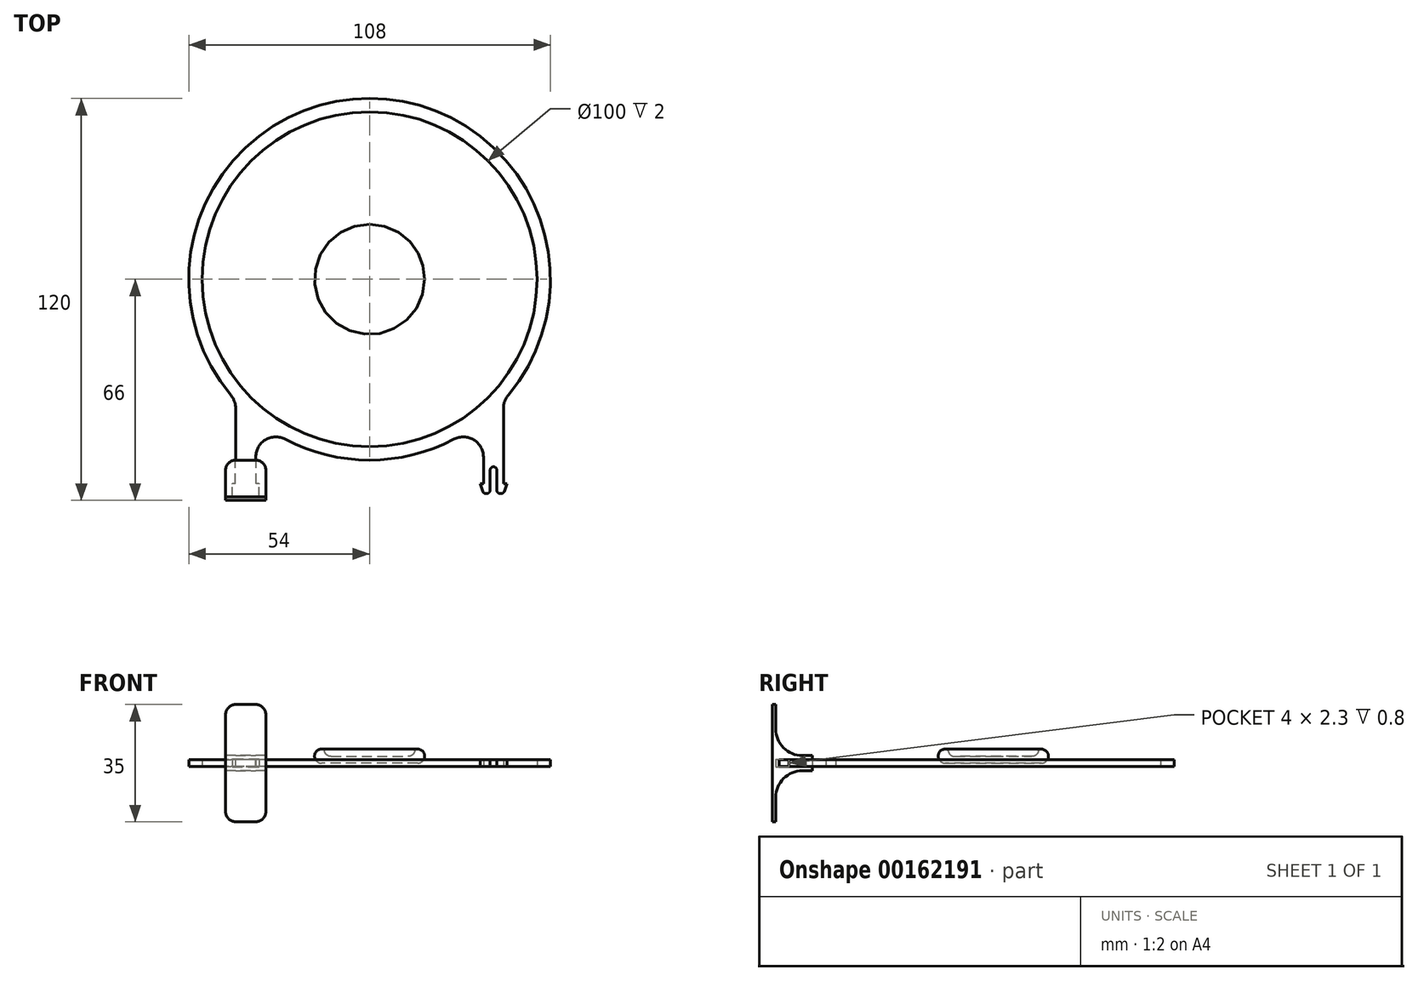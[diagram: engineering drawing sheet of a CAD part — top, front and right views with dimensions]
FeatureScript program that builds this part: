
annotation { "Feature Type Name" : "Feature", "Feature Type Description" : "" }
export const myFeature = defineFeature(function(context is Context, id is Id, definition is map)
    precondition{}
    {
        {
            var Q0;
            Q0=qCreatedBy(makeId("Front.planeOp"),FACE);
            var sketch = newSketch(context, id + "F0", { "sketchPlane" : qUnion([Q0])});
            skLineSegment(sketch, "E0", {"start": v(0, 0) * mm, "end": v(-14.35, 0) * mm});
            skArc(sketch, "E1", {"start": v(-14.35, 4.2) * mm, "mid": v(-16.45, 2.1) * mm, "end": v(-14.35, 0) * mm});
            skLineSegment(sketch, "E2", {"start": v(-14.35, 4.2) * mm, "end": v(-13.5, 4.2) * mm});
            skLineSegment(sketch, "E3", {"start": v(-13.5, 4.2) * mm, "end": v(-13.5, 2) * mm});
            skLineSegment(sketch, "E4", {"start": v(-13.5, 2) * mm, "end": v(0, 2) * mm});
            skLineSegment(sketch, "E5", {"start": v(0, 2) * mm, "end": v(0, 0) * mm});
            skSolve(sketch);
        }
        {
            var Q0;
            Q0=makeQuery(id+"F0.imprint","IMPRINT",FACE,{"disambiguationData":[TD([[makeQuery(id+"F0.imprint","IMPRINT",EDGE,{"derivedFrom":sQuery(id+"F0.wireOp",EDGE,"E0")}),-1.0]])]});
            var Q1;
            Q1=sQuery(id+"F0.wireOp",EDGE,"E5");
            revolve(context, id + "F1", {"entities" : qUnion([Q0]), "axis" : qUnion([Q1]), "revolveType" : RevolveType.FULL});
        }
        {
            var Q0;
            Q0=makeQuery(id+"F1.opRevolve","SWEPT_EDGE",EDGE,{"disambiguationData":[OSD([sQuery(id+"F0.wireOp",EDGE,"E2"),sQuery(id+"F0.wireOp",EDGE,"E3")])]});
            fillet(context, id + "F2", {"entities" : qUnion([Q0]), "radius" : .5 * mm, "tangentPropagation" : true, "allowEdgeOverflow" : false});
        }
        {
            var Q0;
            Q0=makeQuery(id+"F1.opRevolve","SWEPT_EDGE",EDGE,{"disambiguationData":[OSD([sQuery(id+"F0.wireOp",EDGE,"E3"),sQuery(id+"F0.wireOp",EDGE,"E4")])]});
            fillet(context, id + "F3", {"entities" : qUnion([Q0]), "radius" : 2 * mm, "tangentPropagation" : true, "allowEdgeOverflow" : false});
        }
        {
            var Q0;
            Q0=qCreatedBy(makeId("Top.planeOp"),FACE);
            var sketch = newSketch(context, id + "F4", { "sketchPlane" : qUnion([Q0])});
            skCircle(sketch, "E6", {"center": v(0, 0) * mm, "radius": 50 * mm});
            skCircle(sketch, "E7.0", {"center": v(0, 0) * mm, "radius": 54 * mm});
            skLineSegment(sketch, "E8", {"start": v(-40, -36.28) * mm, "end": v(-40, -61) * mm});
            skLineSegment(sketch, "E9", {"start": v(-39.28, -64) * mm, "end": v(-39, -64) * mm});
            skLineSegment(sketch, "E10", {"start": v(-38, -63) * mm, "end": v(-38, -57) * mm});
            skLineSegment(sketch, "E11", {"start": v(-37, -56) * mm, "end": v(-37, -56) * mm});
            skLineSegment(sketch, "E12", {"start": v(-36, -57) * mm, "end": v(-36, -63) * mm});
            skLineSegment(sketch, "E13", {"start": v(-35, -64) * mm, "end": v(-34.72, -64) * mm});
            skLineSegment(sketch, "E14", {"start": v(-34, -61) * mm, "end": v(-34, -41.95) * mm});
            skLineSegment(sketch, "E15", {"start": v(-40, -64.59) * mm, "end": v(-40, -64.59) * mm});
            skLineSegment(sketch, "E16", {"start": v(-40, -61) * mm, "end": v(-41, -61) * mm});
            skLineSegment(sketch, "E17", {"start": v(-41, -61) * mm, "end": v(-40.23, -63.32) * mm});
            skLineSegment(sketch, "E18", {"start": v(-37, -56) * mm, "end": v(-37, -64) * mm, "construction": true});
            skLineSegment(sketch, "E19.MirrorCS", {"start": v(-33, -61) * mm, "end": v(-34, -64) * mm});
            skLineSegment(sketch, "E20.MirrorCS", {"start": v(-33, -61) * mm, "end": v(-33.77, -63.32) * mm});
            skLineSegment(sketch, "E21.MirrorCS", {"start": v(-34, -61) * mm, "end": v(-33, -61) * mm});
            skLineSegment(sketch, "E22", {"start": v(0, 0) * mm, "end": v(0, -62.97) * mm, "construction": true});
            skPoint(sketch, "E23.visualSharp", {"position": v(-38, -56) * mm});
            skArc(sketch, "E23.filletArc", {"start": v(-37, -56) * mm, "mid": v(-37.7, -56.3) * mm, "end": v(-38, -57) * mm});
            skPoint(sketch, "E24.visualSharp", {"position": v(-36, -56) * mm});
            skArc(sketch, "E24.filletArc", {"start": v(-36, -57) * mm, "mid": v(-36.3, -56.3) * mm, "end": v(-37, -56) * mm});
            skPoint(sketch, "E25.visualSharp", {"position": v(-38, -64) * mm});
            skArc(sketch, "E25.filletArc", {"start": v(-39, -64) * mm, "mid": v(-38.3, -63.7) * mm, "end": v(-38, -63) * mm});
            skPoint(sketch, "E26.visualSharp", {"position": v(-40, -64) * mm});
            skArc(sketch, "E26.filletArc", {"start": v(-40.23, -63.32) * mm, "mid": v(-39.86, -63.81) * mm, "end": v(-39.28, -64) * mm});
            skPoint(sketch, "E27.visualSharp", {"position": v(-36, -64) * mm});
            skArc(sketch, "E27.filletArc", {"start": v(-36, -63) * mm, "mid": v(-35.7, -63.7) * mm, "end": v(-35, -64) * mm});
            skPoint(sketch, "E28.visualSharp", {"position": v(-34, -64) * mm});
            skArc(sketch, "E28.filletArc", {"start": v(-34.72, -64) * mm, "mid": v(-34.14, -63.81) * mm, "end": v(-33.77, -63.32) * mm});
            skLineSegment(sketch, "E29.MirrorCS", {"start": v(36, -57) * mm, "end": v(36, -63) * mm});
            skPoint(sketch, "E30.MirrorP", {"position": v(38, -64) * mm});
            skLineSegment(sketch, "E31.MirrorCS", {"start": v(33, -61) * mm, "end": v(34, -64) * mm});
            skLineSegment(sketch, "E32.MirrorCS", {"start": v(40, -36.28) * mm, "end": v(40, -61) * mm});
            skArc(sketch, "E33.MirrorCS", {"start": v(36, -57) * mm, "mid": v(36.3, -56.3) * mm, "end": v(37, -56) * mm});
            skLineSegment(sketch, "E34.MirrorCS", {"start": v(40, -61) * mm, "end": v(41, -61) * mm});
            skLineSegment(sketch, "E35.MirrorCS", {"start": v(35, -64) * mm, "end": v(34.72, -64) * mm});
            skLineSegment(sketch, "E36.MirrorCS", {"start": v(34, -61) * mm, "end": v(33, -61) * mm});
            skArc(sketch, "E37.MirrorCS", {"start": v(40.23, -63.32) * mm, "mid": v(39.86, -63.81) * mm, "end": v(39.28, -64) * mm});
            skLineSegment(sketch, "E38.MirrorCS", {"start": v(33, -61) * mm, "end": v(33.77, -63.32) * mm});
            skLineSegment(sketch, "E39.MirrorCS", {"start": v(39.28, -64) * mm, "end": v(39, -64) * mm});
            skPoint(sketch, "E40.MirrorP", {"position": v(40, -64) * mm});
            skLineSegment(sketch, "E41.MirrorCS", {"start": v(41, -61) * mm, "end": v(40.23, -63.32) * mm});
            skArc(sketch, "E42.MirrorCS", {"start": v(37, -56) * mm, "mid": v(37.7, -56.3) * mm, "end": v(38, -57) * mm});
            skArc(sketch, "E43.MirrorCS", {"start": v(34.72, -64) * mm, "mid": v(34.14, -63.81) * mm, "end": v(33.77, -63.32) * mm});
            skPoint(sketch, "E44.MirrorP", {"position": v(36, -64) * mm});
            skLineSegment(sketch, "E45.MirrorCS", {"start": v(38, -63) * mm, "end": v(38, -57) * mm});
            skPoint(sketch, "E46.MirrorP", {"position": v(38, -56) * mm});
            skArc(sketch, "E47.MirrorCS", {"start": v(39, -64) * mm, "mid": v(38.3, -63.7) * mm, "end": v(38, -63) * mm});
            skLineSegment(sketch, "E48.MirrorCS", {"start": v(37, -56) * mm, "end": v(37, -64) * mm, "construction": true});
            skPoint(sketch, "E49.MirrorP", {"position": v(34, -64) * mm});
            skLineSegment(sketch, "E50.MirrorCS", {"start": v(34, -61) * mm, "end": v(34, -41.95) * mm});
            skPoint(sketch, "E51.MirrorP", {"position": v(36, -56) * mm});
            skArc(sketch, "E52.MirrorCS", {"start": v(36, -63) * mm, "mid": v(35.7, -63.7) * mm, "end": v(35, -64) * mm});
            skSolve(sketch);
        }
        {
            var Q0;
            Q0=makeQuery(id+"F4.imprint","IMPRINT",FACE,{"disambiguationData":[TD([[makeQuery(id+"F4.imprint","IMPRINT",EDGE,{"derivedFrom":sQuery(id+"F4.wireOp",EDGE,"E6")}),-1.0]])]});
            var Q1;
            {var subQ1=sQuery(id+"F4.wireOp",EDGE,"E8");Q1=makeQuery(id+"F4.imprint","IMPRINT",FACE,{"disambiguationData":[TD([[makeQuery(id+"F4.imprint","IMPRINT",EDGE,{"derivedFrom":subQ1}),1.0]])]});}
            var Q2;
            Q2=makeQuery(id+"F4.imprint","IMPRINT",FACE,{"disambiguationData":[TD([[makeQuery(id+"F4.imprint","IMPRINT",EDGE,{"derivedFrom":sQuery(id+"F4.wireOp",EDGE,"E29.MirrorCS")}),-1.0]])]});
            extrude(context, id + "F5", {"entities" : qUnion([Q0, Q1, Q2]), "endBound" : BoundingType.SYMMETRIC, "depth" : 2 * mm});
        }
        {
            var Q0;
            Q0=makeQuery(id+"F5.opExtrude","SWEPT_EDGE",EDGE,{"disambiguationData":[OSD([sQuery(id+"F4.wireOp",EDGE,"E7.0"),sQuery(id+"F4.wireOp",EDGE,"E14")])]});
            var Q1;
            Q1=makeQuery(id+"F5.opExtrude","SWEPT_EDGE",EDGE,{"disambiguationData":[OSD([sQuery(id+"F4.wireOp",EDGE,"E7.0"),sQuery(id+"F4.wireOp",EDGE,"E8")])]});
            var Q2;
            Q2=makeQuery(id+"F5.opExtrude","SWEPT_EDGE",EDGE,{"disambiguationData":[OSD([sQuery(id+"F4.wireOp",EDGE,"E7.0"),sQuery(id+"F4.wireOp",EDGE,"4878f873-84f6-49e9-9cc4-d92dd95d19830.MirrorCS")])]});
            var Q3;
            Q3=makeQuery(id+"F5.opExtrude","SWEPT_EDGE",EDGE,{"disambiguationData":[OSD([sQuery(id+"F4.wireOp",EDGE,"E7.0"),sQuery(id+"F4.wireOp",EDGE,"32b12c6d-282c-4cf4-9ab3-73add998abeb0.MirrorCS")])]});
            fillet(context, id + "F6", {"entities" : qUnion([Q0, Q1, Q2, Q3]), "radius" : 6 * mm, "tangentPropagation" : true, "allowEdgeOverflow" : false});
        }
        {
            var Q0;
            Q0=qCreatedBy(makeId("Top.planeOp"),FACE);
            var sketch = newSketch(context, id + "F7", { "sketchPlane" : qUnion([Q0])});
            skLineSegment(sketch, "E53.bottom", {"start": v(-43, -66) * mm, "end": v(-31, -66) * mm});
            skLineSegment(sketch, "E53.top", {"start": v(-43, -54) * mm, "end": v(-31, -54) * mm});
            skLineSegment(sketch, "E53.left", {"start": v(-43, -66) * mm, "end": v(-43, -54) * mm});
            skLineSegment(sketch, "E53.right", {"start": v(-31, -66) * mm, "end": v(-31, -54) * mm});
            skPoint(sketch, "E53.middle", {"position": v(-37, -60) * mm});
            skPoint(sketch, "E54", {"position": v(-37, -57) * mm});
            skSolve(sketch);
        }
        {
            var Q0;
            Q0=makeQuery(id+"F7.imprint","IMPRINT",FACE,{"disambiguationData":[TD([[makeQuery(id+"F7.imprint","IMPRINT",EDGE,{"derivedFrom":sQuery(id+"F7.wireOp",EDGE,"E53.bottom")}),1.0]])]});
            extrude(context, id + "F8", {"entities" : qUnion([Q0]), "endBound" : BoundingType.SYMMETRIC, "depth" : 4.5 * mm});
        }
        {
            var Q0;
            Q0=makeQuery(id+"F8.opExtrude","SWEPT_FACE",FACE,{"disambiguationData":[OSD([sQuery(id+"F7.wireOp",EDGE,"E53.top")])]});
            var sketch = newSketch(context, id + "F9", { "sketchPlane" : qUnion([Q0])});
            skLineSegment(sketch, "E55.0", {"start": v(40, 1) * mm, "end": v(40, -1) * mm});
            skLineSegment(sketch, "E56.0", {"start": v(34, 1) * mm, "end": v(34, -1) * mm});
            skLineSegment(sketch, "E57", {"start": v(40, 1) * mm, "end": v(34, 1) * mm});
            skLineSegment(sketch, "E58", {"start": v(34, -1) * mm, "end": v(40, -1) * mm});
            skLineSegment(sketch, "E59.0", {"start": v(40.15, 1.15) * mm, "end": v(33.85, 1.15) * mm});
            skLineSegment(sketch, "E59.1", {"start": v(40.15, 1.15) * mm, "end": v(40.15, -1.15) * mm});
            skLineSegment(sketch, "E59.2", {"start": v(33.85, -1.15) * mm, "end": v(40.15, -1.15) * mm});
            skLineSegment(sketch, "E59.3", {"start": v(33.85, 1.15) * mm, "end": v(33.85, -1.15) * mm});
            skLineSegment(sketch, "E60", {"start": v(33.85, 1.15) * mm, "end": v(33.05, 1.15) * mm});
            skLineSegment(sketch, "E61", {"start": v(33.05, 1.15) * mm, "end": v(33.05, -1.15) * mm});
            skLineSegment(sketch, "E62", {"start": v(33.05, -1.15) * mm, "end": v(33.85, -1.15) * mm});
            skLineSegment(sketch, "E63", {"start": v(37, 1) * mm, "end": v(37, -1) * mm, "construction": true});
            skLineSegment(sketch, "E64.MirrorCS", {"start": v(40.15, 1.15) * mm, "end": v(40.95, 1.15) * mm});
            skLineSegment(sketch, "E65.MirrorCS", {"start": v(40.95, 1.15) * mm, "end": v(40.95, -1.15) * mm});
            skLineSegment(sketch, "E66.MirrorCS", {"start": v(40.95, -1.15) * mm, "end": v(40.15, -1.15) * mm});
            skSolve(sketch);
        }
        {
            var Q0;
            Q0=makeQuery(id+"F9.imprint","IMPRINT",FACE,{"disambiguationData":[TD([[makeQuery(id+"F9.imprint","IMPRINT",EDGE,{"derivedFrom":sQuery(id+"F9.wireOp",EDGE,"E55.0")}),-1.0]])]});
            var Q1;
            Q1=makeQuery(id+"F9.imprint","IMPRINT",FACE,{"disambiguationData":[TD([[makeQuery(id+"F9.imprint","IMPRINT",EDGE,{"derivedFrom":sQuery(id+"F9.wireOp",EDGE,"E55.0")}),1.0]])]});
            extrude(context, id + "F10", {"entities" : qUnion([Q0, Q1]), "operationType" : NewBodyOperationType.REMOVE, "oppositeDirection" : true, "depth" : 7 * mm});
        }
        {
            var Q0;
            Q0=makeQuery(id+"F9.imprint","IMPRINT",FACE,{"disambiguationData":[TD([[makeQuery(id+"F9.imprint","IMPRINT",EDGE,{"derivedFrom":sQuery(id+"F9.wireOp",EDGE,"E59.1")}),1.0]])]});
            var Q1;
            Q1=makeQuery(id+"F9.imprint","IMPRINT",FACE,{"disambiguationData":[TD([[makeQuery(id+"F9.imprint","IMPRINT",EDGE,{"derivedFrom":sQuery(id+"F9.wireOp",EDGE,"E55.0")}),1.0]])]});
            var Q2;
            Q2=makeQuery(id+"F9.imprint","IMPRINT",FACE,{"disambiguationData":[TD([[makeQuery(id+"F9.imprint","IMPRINT",EDGE,{"derivedFrom":sQuery(id+"F9.wireOp",EDGE,"E55.0")}),-1.0]])]});
            var Q3;
            Q3=makeQuery(id+"F9.imprint","IMPRINT",FACE,{"disambiguationData":[TD([[makeQuery(id+"F9.imprint","IMPRINT",EDGE,{"derivedFrom":sQuery(id+"F9.wireOp",EDGE,"E59.3")}),-1.0]])]});
            extrude(context, id + "F11", {"entities" : qUnion([Q0, Q1, Q2, Q3]), "operationType" : NewBodyOperationType.REMOVE, "oppositeDirection" : true, "depth" : 11 * mm, "hasSecondDirection" : true, "secondDirectionOppositeDirection" : true, "secondDirectionDepth" : 7 * mm});
        }
        {
            var Q0;
            Q0=qCreatedBy(makeId("Top.planeOp"),FACE);
            var sketch = newSketch(context, id + "F12", { "sketchPlane" : qUnion([Q0])});
            skLineSegment(sketch, "E67", {"start": v(-43, -65) * mm, "end": v(-31, -65) * mm});
            skLineSegment(sketch, "E68.0", {"start": v(-43, -66) * mm, "end": v(-31, -66) * mm});
            skLineSegment(sketch, "E69", {"start": v(-43, -66) * mm, "end": v(-43, -65) * mm});
            skLineSegment(sketch, "E70", {"start": v(-31, -66) * mm, "end": v(-31, -65) * mm});
            skSolve(sketch);
        }
        {
            var Q0;
            Q0=qSketchRegion(id+"F12",true);
            extrude(context, id + "F13", {"entities" : qUnion([Q0]), "operationType" : NewBodyOperationType.ADD, "endBound" : BoundingType.SYMMETRIC, "depth" : 35 * mm});
        }
        {
            var Q0;
            Q0=makeQuery(id+"F13.boolean.opBoolean","INTERSECT",EDGE,{"derivedFrom":[makeQuery(id+"F8.opExtrude","CAP_FACE",FACE,{"disambiguationData":[OSD([sQuery(id+"F7.wireOp",EDGE,"E53.bottom"),sQuery(id+"F7.wireOp",EDGE,"E53.top"),sQuery(id+"F7.wireOp",EDGE,"E53.left"),sQuery(id+"F7.wireOp",EDGE,"E53.right")])],"isStart":true}),makeQuery(id+"F13.opExtrude","SWEPT_FACE",FACE,{"disambiguationData":[OSD([sQuery(id+"F12.wireOp",EDGE,"E67")])]})]});
            var Q1;
            Q1=makeQuery(id+"F13.boolean.opBoolean","INTERSECT",EDGE,{"derivedFrom":[makeQuery(id+"F8.opExtrude","CAP_FACE",FACE,{"disambiguationData":[OSD([sQuery(id+"F7.wireOp",EDGE,"E53.bottom"),sQuery(id+"F7.wireOp",EDGE,"E53.top"),sQuery(id+"F7.wireOp",EDGE,"E53.left"),sQuery(id+"F7.wireOp",EDGE,"E53.right")])],"isStart":false}),makeQuery(id+"F13.opExtrude","SWEPT_FACE",FACE,{"disambiguationData":[OSD([sQuery(id+"F12.wireOp",EDGE,"E67")])]})]});
            fillet(context, id + "F14", {"entities" : qUnion([Q0, Q1]), "radius" : 8 * mm, "tangentPropagation" : true, "allowEdgeOverflow" : false});
        }
        {
            var Q0;
            Q0=makeQuery(id+"F8.opExtrude","SWEPT_EDGE",EDGE,{"disambiguationData":[OSD([sQuery(id+"F7.wireOp",EDGE,"E53.top"),sQuery(id+"F7.wireOp",EDGE,"E53.right")])]});
            var Q1;
            Q1=makeQuery(id+"F8.opExtrude","SWEPT_EDGE",EDGE,{"disambiguationData":[OSD([sQuery(id+"F7.wireOp",EDGE,"E53.top"),sQuery(id+"F7.wireOp",EDGE,"E53.left")])]});
            var Q2;
            Q2=makeQuery(id+"F13.opExtrude","CAP_EDGE",EDGE,{"disambiguationData":[OSD([sQuery(id+"F12.wireOp",EDGE,"E69")])],"isStart":false});
            var Q3;
            Q3=makeQuery(id+"F13.opExtrude","CAP_EDGE",EDGE,{"disambiguationData":[OSD([sQuery(id+"F12.wireOp",EDGE,"E70")])],"isStart":false});
            var Q4;
            Q4=makeQuery(id+"F13.opExtrude","CAP_EDGE",EDGE,{"disambiguationData":[OSD([sQuery(id+"F12.wireOp",EDGE,"E69")])],"isStart":true});
            var Q5;
            Q5=makeQuery(id+"F13.opExtrude","CAP_EDGE",EDGE,{"disambiguationData":[OSD([sQuery(id+"F12.wireOp",EDGE,"E70")])],"isStart":true});
            fillet(context, id + "F15", {"entities" : qUnion([Q0, Q1, Q2, Q3, Q4, Q5]), "radius" : 3 * mm, "tangentPropagation" : true, "allowEdgeOverflow" : false});
        }
    });
